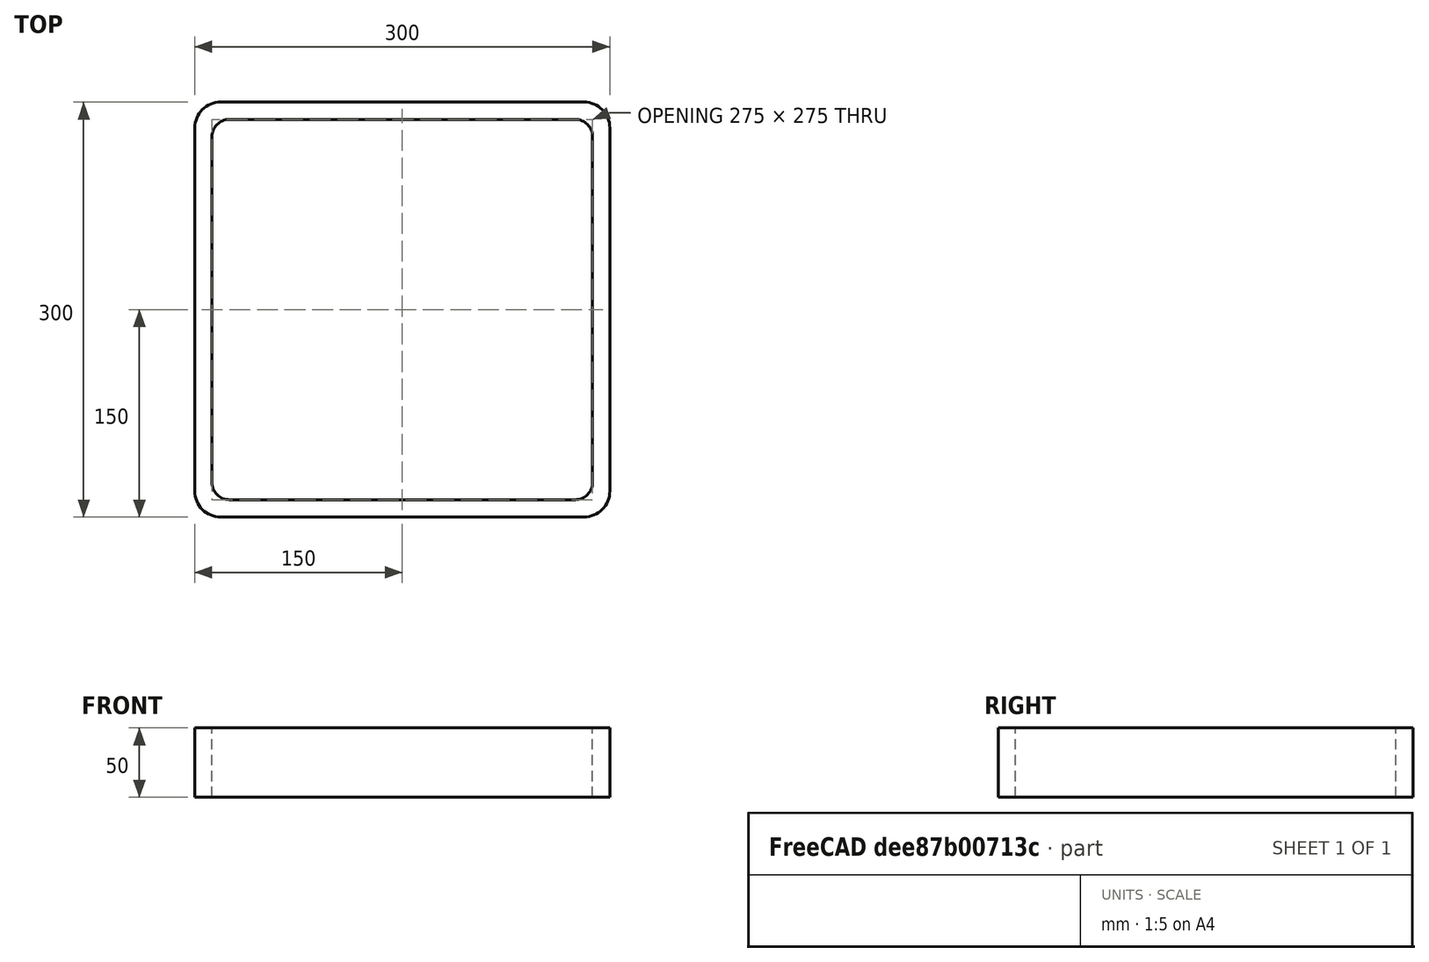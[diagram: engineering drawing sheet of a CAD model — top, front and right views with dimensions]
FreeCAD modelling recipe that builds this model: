
FCSTD DOCUMENT  (FreeCAD 0.15R4671 (Git))
Label: Square hollow section 300x300x12.5 EN10219 S235JRH
License: All rights reserved
LicenseURL: http://en.wikipedia.org/wiki/All_rights_reserved
objects: Sketcher::SketchObject×1, Part::Extrusion×1
note: 2 computed .brp shape members not serialized (recipe doc carries the construction recipe); baked Part::Feature solids carry a one-line shape summary decoded from their .brp

FEATURE [Sketcher::SketchObject] Sketch
  sketch-geometry (16):
    g0: LineSegment StartX=-125 StartY=137.5 StartZ=0 EndX=125 EndY=137.5 EndZ=0
    g1: LineSegment StartX=137.5 StartY=125 StartZ=0 EndX=137.5 EndY=-125 EndZ=0
    g2: LineSegment StartX=125 StartY=-137.5 StartZ=0 EndX=-125 EndY=-137.5 EndZ=0
    g3: LineSegment StartX=-137.5 StartY=-125 StartZ=0 EndX=-137.5 EndY=125 EndZ=0
    g4: LineSegment StartX=-131.25 StartY=150 StartZ=0 EndX=131.25 EndY=150 EndZ=0
    g5: LineSegment StartX=150 StartY=131.25 StartZ=0 EndX=150 EndY=-131.25 EndZ=0
    g6: LineSegment StartX=131.25 StartY=-150 StartZ=0 EndX=-131.25 EndY=-150 EndZ=0
    g7: LineSegment StartX=-150 StartY=-131.25 StartZ=0 EndX=-150 EndY=131.25 EndZ=0
    g8: ArcOfCircle CenterX=-125 CenterY=125 CenterZ=0 NormalX=0 NormalY=0 NormalZ=1 Radius=12.5 StartAngle=1.5708 EndAngle=3.14159
    g9: ArcOfCircle CenterX=125 CenterY=125 CenterZ=0 NormalX=0 NormalY=0 NormalZ=1 Radius=12.5 StartAngle=0 EndAngle=1.5708
    g10: ArcOfCircle CenterX=125 CenterY=-125 CenterZ=0 NormalX=0 NormalY=0 NormalZ=1 Radius=12.5 StartAngle=4.71239 EndAngle=6.28319
    g11: ArcOfCircle CenterX=-125 CenterY=-125 CenterZ=0 NormalX=0 NormalY=0 NormalZ=1 Radius=12.5 StartAngle=3.14159 EndAngle=4.71239
    g12: ArcOfCircle CenterX=131.25 CenterY=131.25 CenterZ=0 NormalX=0 NormalY=0 NormalZ=1 Radius=18.75 StartAngle=0 EndAngle=1.5708
    g13: ArcOfCircle CenterX=131.25 CenterY=-131.25 CenterZ=0 NormalX=0 NormalY=0 NormalZ=1 Radius=18.75 StartAngle=4.71239 EndAngle=6.28319
    g14: ArcOfCircle CenterX=-131.25 CenterY=-131.25 CenterZ=0 NormalX=0 NormalY=0 NormalZ=1 Radius=18.75 StartAngle=3.14159 EndAngle=4.71239
    g15: ArcOfCircle CenterX=-131.25 CenterY=131.25 CenterZ=0 NormalX=0 NormalY=0 NormalZ=1 Radius=18.75 StartAngle=1.5708 EndAngle=3.14159
  constraints (36):
    c: Horizontal(g2)
    c: Vertical(g3)
    c: Horizontal(g6)
    c: Vertical(g7)
    c: Tangent(g3,g8) = 1.5708
    c: Tangent(g0,g8) = 1.5708
    c: Tangent(g0,g9) = 1.5708
    c: Tangent(g1,g9) = 1.5708
    c: Tangent(g1,g10) = 1.5708
    c: Tangent(g2,g10) = 1.5708
    c: Tangent(g2,g11) = 1.5708
    c: Tangent(g3,g11) = 1.5708
    c: Tangent(g4,g12) = 1.5708
    c: Tangent(g5,g12) = 1.5708
    c: Tangent(g5,g13) = 1.5708
    c: Tangent(g6,g13) = 1.5708
    c: Tangent(g6,g14) = 1.5708
    c: Tangent(g7,g14) = 1.5708
    c: Tangent(g7,g15) = 1.5708
    c: Tangent(g4,g15) = 1.5708
    c: Equal(g9,g8)
    c: Equal(g9,g11)
    c: Equal(g9,g10)
    c: Equal(g12,g15)
    c: Equal(g12,g14)
    c: Equal(g12,g13)
    c: Symmetric(g4,g6,g-1)
    c: Symmetric(g7,g5,g-2)
    c: DistanceY(g4,g6) = -300
    c: DistanceX(g7,g5) = 300
    c: Symmetric(g3,g1,g-2)
    c: Symmetric(g0,g2,g-1)
    c: DistanceY(g0,g4) = 12.5
    c: DistanceX(g5,g1) = -12.5
    c: Radius(g9) = 12.5
    c: Radius(g12) = 18.75
FEATURE [Part::Extrusion] Extrude  label="Square hollow section 300x300x12.5 EN10219 S235JRH"
  Base = -> Sketch
  Dir = (0,0,50)
  Solid = true
